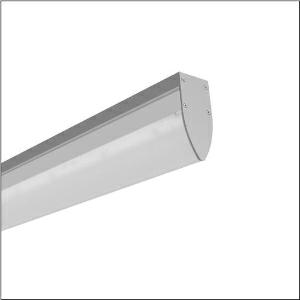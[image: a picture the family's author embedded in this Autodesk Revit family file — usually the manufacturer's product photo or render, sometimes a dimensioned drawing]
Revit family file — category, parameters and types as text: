
# Revit family: mira_r__21_td_51fr527p494a_f38a
name_source: partatom
category: Lighting Fixtures
units: mm (PartAtom-declared; Revit-internal decimal feet)

## family parameters
Cut with Voids When Loaded = No
Host = Face
Light Source = No
Part Type = Normal
Room Calculation Point = No
Round Connector Dimension = Use Diameter
Shared = No

## types (1)
- Mira® 21 TD (1 x LED, 9160 lm, 65 W, 4000K)
    Apparent Load = 65 VA
    CIE Flux Codes = 40 68 87 81 100
    Color Rendering = 80
    Color Temperature = 4000K
    Default Elevation = 1800 mm
    Description = Mira® 21 TD, clean room luminaire, primary light control with reflector, primary optical cover: cover, of PMMA, frosted, light emission: direct distribution, primary light characteristic: symmetric, installation type: surface-mounted, LED, rated luminous flux: 9.160lm, luminous efficacy: 141lm/W, light colour: 840, colour temperature: 4000K, control gear: ECG, with terminal, 3-pole, max. 2.5mm², mains connection: 230V, AC, 50/60Hz, rated input power: 65W, luminaire housing, of sheet steel, coated, pure white (RAL 9010), length: 1.500mm, width: 55mm, height: 120mm, protection rating (complete): IP43, insulation class (complete): insulation class I (protective earthing), certification: CE, UKCA, permissible operating ambient temperature: -5..+40°C, standard: EN 50419, packaging unit: 1 piece
    Height = 0 mm  [stored 0 ft]
    Lamp = 1 x LED
    Lamp Light Flux = 9160 lm
    Lamp Power = 65 W
    Lamp count = 1
    Length = 1500 mm
    Luminous efficacy = 141 lm/W
    Manufacturer = Siteco
    ModVariant = No
    Model = 51FR527P494A
    Mounting Place = Ceiling
    Mounting Type = Recessed
    Number of Poles = 1
    OnlyDefault = Yes
    Power Factor = 1
    Product Name = Mira® 21 TD
    Product group = clean room luminaire
    ProductGroupID = 402
    Protection Class = Protection class I
    Protection Degree = IP 43
    RLX_Detail_Level = 1
    RLX_Emergency_Light_Flux = 0 lm
    RLX_Emergency_Type = 0
    RLX_Emergency_Type_DB = No
    RlxData = <blob elided: 25165 chars, md5=75f39b39>
    Socket = socket
    Standby Power = 0 W
    System Light Flux = 9160 lm
    System Power = 65 W
    Type Comments = Product without accessories
    Type Image = l_1007115.jpg
    URL = http://relux.com
    VarID = ---
    Voltage = 0 V
    Weight = 0.00 kg
    Width = 55 mm

note: [stored X ft] marks values corroborated as IEEE doubles in the binary element streams (Revit-internal decimal feet)

## geometry (parser evidence)
native form markers: Blend x4, Sweep x12
no freeform markers — native parametric forms only
